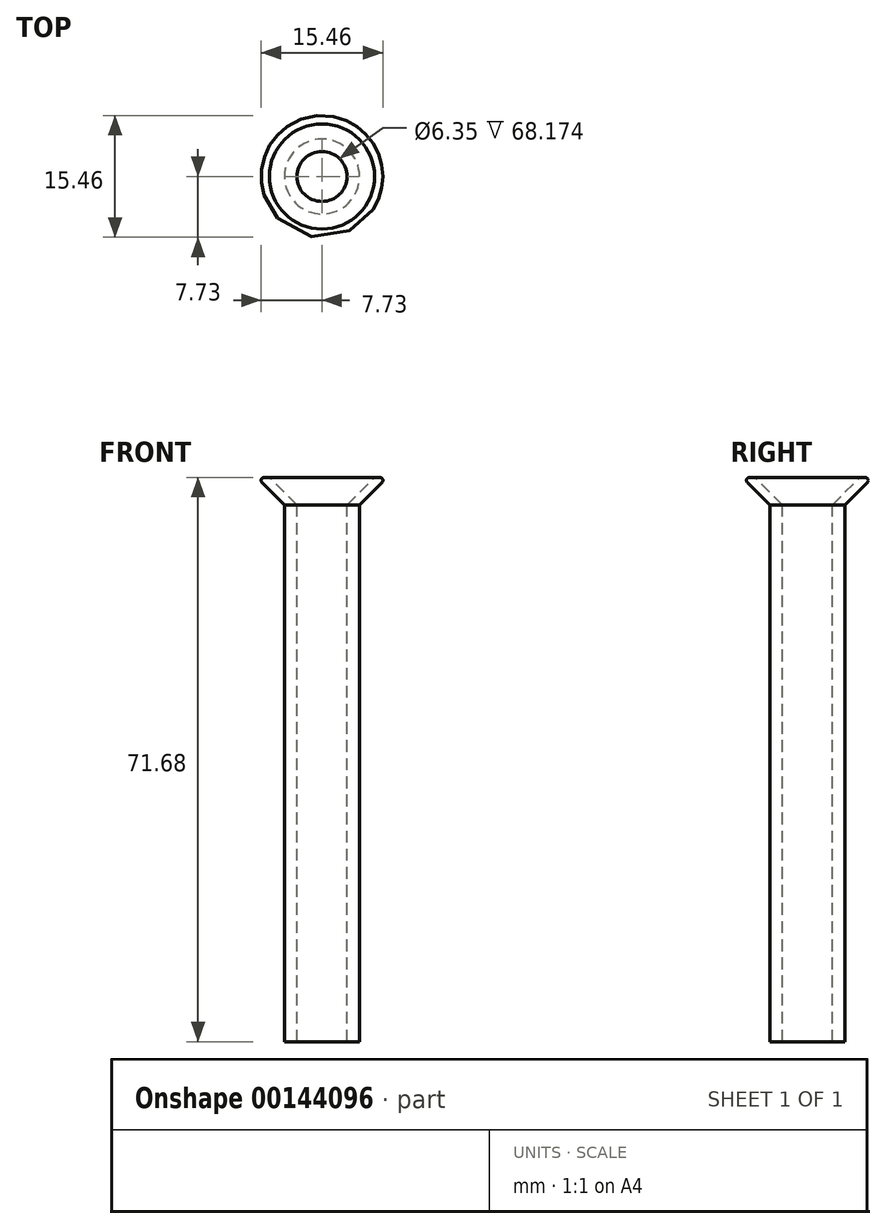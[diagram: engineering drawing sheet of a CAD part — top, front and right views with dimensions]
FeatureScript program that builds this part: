
annotation { "Feature Type Name" : "Feature", "Feature Type Description" : "" }
export const myFeature = defineFeature(function(context is Context, id is Id, definition is map)
    precondition{}
    {
        {
            var Q0;
            Q0=qCreatedBy(makeId("Right.planeOp"),FACE);
            var sketch = newSketch(context, id + "F0", { "sketchPlane" : qUnion([Q0])});
            skLineSegment(sketch, "E0", {"start": v(0, 0) * mm, "end": v(0, -30.5) * mm});
            skLineSegment(sketch, "E1", {"start": v(3.18, 0) * mm, "end": v(3.18, 68.17) * mm});
            skLineSegment(sketch, "E2", {"start": v(3.18, 0) * mm, "end": v(4.76, 0) * mm});
            skLineSegment(sketch, "E3", {"start": v(4.76, 0) * mm, "end": v(4.76, 68.17) * mm});
            skLineSegment(sketch, "E4", {"start": v(4.76, 68.17) * mm, "end": v(8.27, 71.68) * mm});
            skLineSegment(sketch, "E5", {"start": v(3.17, 68.17) * mm, "end": v(6.68, 71.68) * mm});
            skLineSegment(sketch, "E6", {"start": v(6.68, 71.68) * mm, "end": v(8.27, 71.68) * mm});
            skPoint(sketch, "E7.orphan", {"position": v(0, 71.68) * mm});
            skSolve(sketch);
        }
        {
            var Q0;
            Q0=makeQuery(id+"F0.imprint","IMPRINT",FACE,{"disambiguationData":[TD([[makeQuery(id+"F0.imprint","IMPRINT",EDGE,{"derivedFrom":sQuery(id+"F0.wireOp",EDGE,"E1")}),-1.0]])]});
            var Q1;
            Q1=sQuery(id+"F0.wireOp",EDGE,"E0");
            revolve(context, id + "F1", {"entities" : qUnion([Q0]), "axis" : qUnion([Q1]), "revolveType" : RevolveType.FULL});
        }
        {
            var Q0;
            Q0=makeQuery(id+"F1.opRevolve","SWEPT_EDGE",EDGE,{"disambiguationData":[OSD([sQuery(id+"F0.wireOp",EDGE,"E4"),sQuery(id+"F0.wireOp",EDGE,"E6")])]});
            fillet(context, id + "F2", {"entities" : qUnion([Q0]), "radius" : 0.38 * mm, "tangentPropagation" : true, "allowEdgeOverflow" : false});
        }
    });
